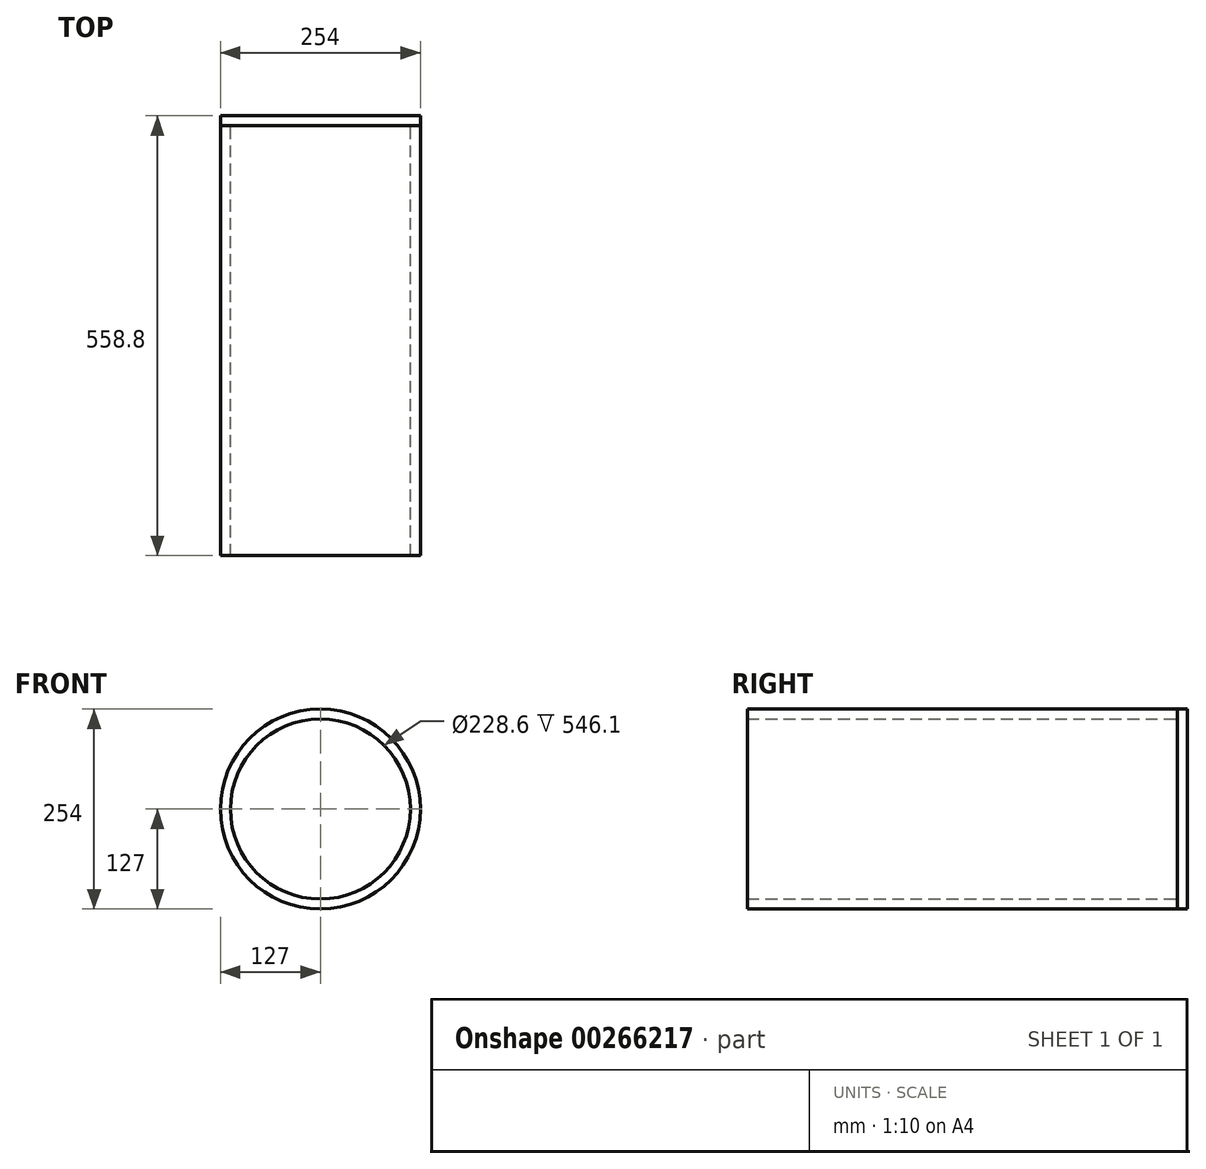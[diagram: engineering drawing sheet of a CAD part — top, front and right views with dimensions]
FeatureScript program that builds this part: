
annotation { "Feature Type Name" : "Feature", "Feature Type Description" : "" }
export const myFeature = defineFeature(function(context is Context, id is Id, definition is map)
    precondition{}
    {
        {
            var Q0;
            Q0=qCreatedBy(makeId("Front.planeOp"),FACE);
            var sketch = newSketch(context, id + "F0", { "sketchPlane" : qUnion([Q0])});
            skCircle(sketch, "E0", {"center": v(0, 0) * mm, "radius": 127 * mm});
            skCircle(sketch, "E1", {"center": v(0, 0) * mm, "radius": 114.3 * mm});
            skSolve(sketch);
        }
        {
            var Q0;
            Q0 = qSketchRegion(id + "F0", true);
            extrude(context, id + "F1", {"entities" : qUnion([Q0]), "depth" : 546.1 * mm});
        }
        {
            var Q0;
            Q0=makeQuery(id+"F0.imprint","IMPRINT",FACE,{"disambiguationData":[TD([[makeQuery(id+"F0.imprint","IMPRINT",EDGE,{"derivedFrom":sQuery(id+"F0.wireOp",EDGE,"E1")}),1.0]])]});
            var Q1;
            Q1=makeQuery(id+"F0.imprint","IMPRINT",FACE,{"disambiguationData":[TD([[makeQuery(id+"F0.imprint","IMPRINT",EDGE,{"derivedFrom":sQuery(id+"F0.wireOp",EDGE,"E0")}),1.0]])]});
            extrude(context, id + "F2", {"entities" : qUnion([Q0, Q1]), "oppositeDirection" : true, "depth" : 12.7 * mm});
        }
    });
